# Revit family: Stonepanel_Sabbia_ESP
name_source: partatom
category: Modelos genéricos
revit_build: Autodesk Revit LT 2017 (Build: 20160225_1515(x64)
units: mm (PartAtom-declared; Revit-internal decimal feet)

## family parameters
Anfitrión = Muro
Compartido = No
Corte con vacíos al cargar = No
Cota de conector redondo = Diámetro de uso
Puede alojar armadura = No
Punto de cálculo de habitación = No
Siempre vertical = Sí
Tipo de pieza = Normal

## types (1)
- Stonepanel® Sabbia
    Absorción = Baja absorción
    Acabado = Natural
    Alto = 200 mm  [stored 0.656168 ft]
    Ancho = 50 mm  [stored 0.164042 ft]
    Aspecto = Natural
    Certificaciones = Avis Technique
Resistencia mecánica del anclaje
Resistencia mecánica de la cinta de seguridad
Ensayo de durabilidad tras la acción del agua
Ensayo de durabilidad tras la acción del hielo
Ensayo sísmico
Ensayo de fuego
    Color principal = Crema
    Color secundario = Dorado
    Densidad aparente = 79,5 kg/m2
    Descripción = Pieza de piedra natural montada sobre una base de cemento y reforzada con una malla de fibra de vidrio .
Posee sistema de anclaje patentado, de acero inoxidable, que permite su instalación a más de 2 metros de altura
    Desfase de altura = 0 mm  [stored 0 ft]
    Detalles constructivos = Detalles de:
- Instalación con perfil metálico
- Instalación de Stonepanel
- Instalación en muro interior
- Instalación del elemento de seguridad (cinta perforada + tacos)
- Esquinas entrantes
- Esquinas salientes
- Esquinas salientes pre-fabricadas
- Esquinas salientes mediante serrado del panel
- Esquinas salientes sin continuidad de Stonepanel (caso de una fachada lateral)
- Bordes superiores
- Sobre parapeto
- Marco de vano
    Durabilidad = Según el certificado BBA, el sistema tiene una vida de diseño superior a 30 años.
    Ensayos realizados por Avis Technique = Resistencia mecánica del anclaje, Resistencia mecánica de la cinta de seguridad, Ensayo de durabilidad tras la acción del agua, Ensayo de durabilidad tras la acción del hielo, Ensayo sísmico
    Envejecimiento por cambio térmicos = Sin alteraciones despues de 20 ciclos.
    Fabricante = Cupastone
    Forma = Forma de "s"
    Forma de suministro = Los paneles se presentan en parejas, en un embalaje plástico de 2 piezas.
    Formato = 600 x 200
    H1 = 76 mm  [stored 0.249344 ft]
    Imagen de tipo = <Ninguno>
    Impacto = -
    Largo = 600 mm
    Limpieza = En general, los paneles no requieren mantenimiento y son auto- limpiantes, pero la eliminación de algunos tipos de marcas pueden requerir un tratamiento especializado.
En caso de suciedad anormal, la superficie puede limpiarse con una mezcla / detergente doméstico y agua caliente , aplicada con una almohadilla de limpieza adecuado o una esponja.
    Material = Panel de piedra caliza de tonalidad crema con surcos dorados y color tierra. Se trata de la piedra más clara y luminosa de STONEPANEL®.
    Modelo = Stonepanel® Sabbia
    NBS Reference = 45-25-45/380 Natural stone panels
    Omniclass = 23-15 15 15 11
    Otros datos de interés del producto = Dispone de un anclaje para instalar a alturas superiores a 2 metros
    Oxidación = No oxida
    Peso = 8,75 kg
    Resistencia = Buena resistencia
    Resistencia al fuego = A1 incombustible
    Sistema de anclaje = Cinta perforada en acero inoxidable:
- Naturaleza del acero: AISI 316 (1.4401) o AISI 304 (1.4301)
- Espesor mínimo (mm) : 0,7
- Ancho (mm) : 12 a 15
- Diámetro del hueco (mm) : 6 ± 1

Tacos:
La elección de los tacos y clavijas de fijación debe ser realizada teniendo en cuenta la acción en depresión del viento (muros exteriores) y de la resistencia de los tacos en el soporte, en función de la naturaleza del soporte.
    URL = http://www.cupastone.es
    Uniclass 2 = Pr_25_71_14_56 Natural stone panels
    Uniclass 2015 = Pr_25_71_14_56 Natural stone panels
    Usos Indicados = Revestimiento de Paredes exteriores e interiores en edificaciones nuevas o rehabilitaciones
    Ventajas de Stonepanel = Eficaz: Instalación ágil y sencilla : 10 veces más rápido que la mampostería tradicional (Ritmo medio de colocación de 20 m2/día). Mayor rentabilidad gracias al menor desperdicio de material en obra y a la durabilidad de un producto natural frente a otros revestimientos. La colocación de los paneles no requiere mano de obra ni maquinaria especializada.
Seguro: Un sistema de anclaje patentado, de acero inoxidable, que permite su instalación a más de 2 metros de altura. Base de cemento homogénea y rugosa que garantiza la adhesión y permite el corte sin desprendimiento.
Calidad: Control permanente del proceso de producción desde la oficina I+D+I. Una cuidada selección de piedra natural realizada por los expertos de CUPASTONE. Disponibilidad de piezas especiales para adaptarse perfectamente a cada edificio: esquinas (macizas, rectas, dobles o para ventanas), cubremuros, y otros complementarios.
Estética: Forma de “S” que evita la visión de las juntas para homogenizar el aspecto final. Gran variedad de paneles para elegir entre colores y acabados de piedra natural. La propia belleza y exclusividad de la piedra natural: Cada piedra es
única.

note: [stored X ft] marks values corroborated as IEEE doubles in the binary element streams (Revit-internal decimal feet)
